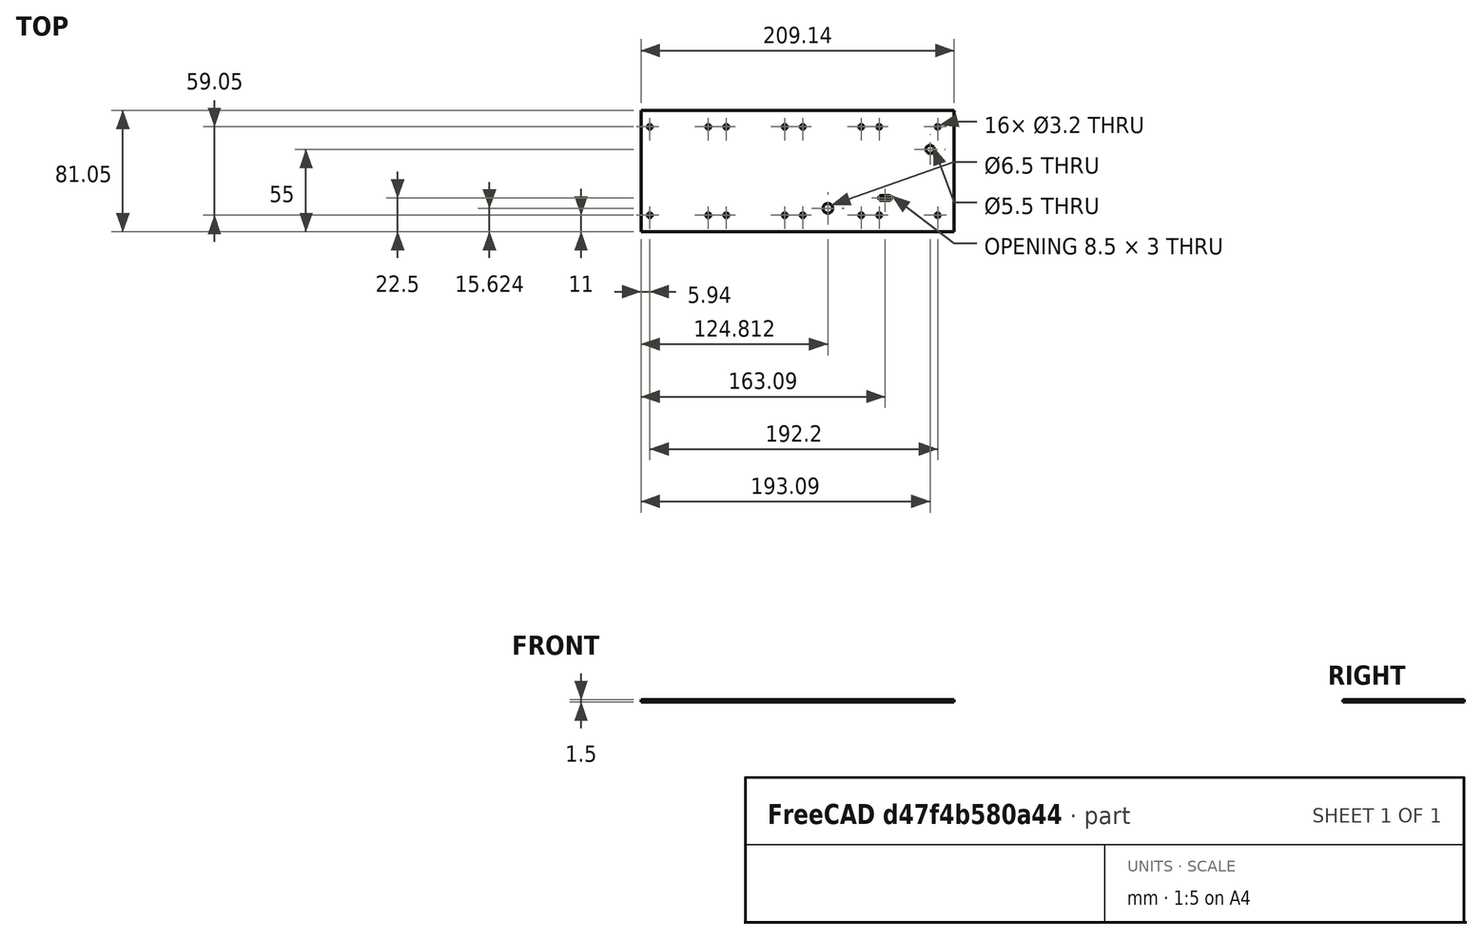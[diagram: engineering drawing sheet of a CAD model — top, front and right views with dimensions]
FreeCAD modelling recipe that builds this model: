
FCSTD DOCUMENT  (FreeCAD 0.21R33694 (Git))
Label: V1
License: All rights reserved
LicenseURL: https://en.wikipedia.org/wiki/All_rights_reserved
objects: Sketcher::SketchObject×1, App::VRMLObject×1, App::Part×1, PartDesign::Pad×1, PartDesign::Body×1
note: 4 computed .brp shape members not serialized (recipe doc carries the construction recipe); baked Part::Feature solids carry a one-line shape summary decoded from their .brp

FEATURE [Sketcher::SketchObject] Sketch
  FullyConstrained = false
  sketch-geometry (52):
    g0: LineSegment StartX=0 StartY=0 StartZ=0 EndX=209.14 EndY=0 EndZ=0
    g1: LineSegment StartX=209.14 StartY=0 StartZ=0 EndX=209.14 EndY=81.05 EndZ=0
    g2: LineSegment StartX=209.14 StartY=81.05 StartZ=0 EndX=0 EndY=81.05 EndZ=0
    g3: LineSegment StartX=0 StartY=81.05 StartZ=0 EndX=0 EndY=0 EndZ=0
    g4: Circle CenterX=5.94 CenterY=70.05 CenterZ=0 NormalX=0 NormalY=0 NormalZ=1 AngleXU=0 Radius=1.6
    g5: Circle CenterX=44.99 CenterY=70.05 CenterZ=0 NormalX=0 NormalY=0 NormalZ=1 AngleXU=0 Radius=1.6
    g6: Circle CenterX=56.99 CenterY=70.05 CenterZ=0 NormalX=0 NormalY=0 NormalZ=1 AngleXU=0 Radius=1.6
    g7: Circle CenterX=96.04 CenterY=70.05 CenterZ=0 NormalX=0 NormalY=0 NormalZ=1 AngleXU=0 Radius=1.6
    g8: Circle CenterX=108.04 CenterY=70.05 CenterZ=0 NormalX=0 NormalY=0 NormalZ=1 AngleXU=0 Radius=1.6
    g9: Circle CenterX=147.09 CenterY=70.05 CenterZ=0 NormalX=0 NormalY=0 NormalZ=1 AngleXU=0 Radius=1.6
    g10: Circle CenterX=159.09 CenterY=70.05 CenterZ=0 NormalX=0 NormalY=0 NormalZ=1 AngleXU=0 Radius=1.6
    g11: Circle CenterX=198.14 CenterY=70.05 CenterZ=0 NormalX=0 NormalY=0 NormalZ=1 AngleXU=0 Radius=1.6
    g12: LineSegment StartX=0 StartY=70.05 StartZ=0 EndX=209.14 EndY=70.05 EndZ=0
    g13: LineSegment StartX=0 StartY=11 StartZ=0 EndX=209.14 EndY=11 EndZ=0
    g14: LineSegment StartX=5.94 StartY=70.05 StartZ=0 EndX=5.94 EndY=11 EndZ=0
    g15: LineSegment StartX=44.99 StartY=70.05 StartZ=0 EndX=44.99 EndY=11 EndZ=0
    g16: LineSegment StartX=56.99 StartY=70.05 StartZ=0 EndX=56.99 EndY=11 EndZ=0
    g17: LineSegment StartX=96.04 StartY=70.05 StartZ=0 EndX=96.04 EndY=11 EndZ=0
    g18: LineSegment StartX=108.04 StartY=70.05 StartZ=0 EndX=108.04 EndY=11 EndZ=0
    g19: LineSegment StartX=147.09 StartY=70.05 StartZ=0 EndX=147.09 EndY=11 EndZ=0
    g20: LineSegment StartX=159.09 StartY=70.05 StartZ=0 EndX=159.09 EndY=11 EndZ=0
    g21: LineSegment StartX=198.14 StartY=70.05 StartZ=0 EndX=198.14 EndY=11 EndZ=0
    g22: Circle CenterX=198.14 CenterY=11 CenterZ=0 NormalX=0 NormalY=0 NormalZ=1 AngleXU=0 Radius=1.6
    g23: Circle CenterX=159.09 CenterY=11 CenterZ=0 NormalX=0 NormalY=0 NormalZ=1 AngleXU=0 Radius=1.6
    g24: Circle CenterX=147.09 CenterY=11 CenterZ=0 NormalX=0 NormalY=0 NormalZ=1 AngleXU=0 Radius=1.6
    g25: Circle CenterX=108.04 CenterY=11 CenterZ=0 NormalX=0 NormalY=0 NormalZ=1 AngleXU=0 Radius=1.6
    g26: Circle CenterX=96.04 CenterY=11 CenterZ=0 NormalX=0 NormalY=0 NormalZ=1 AngleXU=0 Radius=1.6
    g27: Circle CenterX=56.99 CenterY=11 CenterZ=0 NormalX=0 NormalY=0 NormalZ=1 AngleXU=0 Radius=1.6
    g28: Circle CenterX=44.99 CenterY=11 CenterZ=0 NormalX=0 NormalY=0 NormalZ=1 AngleXU=0 Radius=1.6
    g29: Circle CenterX=5.94 CenterY=11 CenterZ=0 NormalX=0 NormalY=0 NormalZ=1 AngleXU=0 Radius=1.6
    g30: LineSegment StartX=160.09 StartY=21 StartZ=0 EndX=166.09 EndY=21 EndZ=0
    g31: LineSegment StartX=160.09 StartY=24 StartZ=0 EndX=166.09 EndY=24 EndZ=0
    g32: LineSegment StartX=167.34 StartY=22.75 StartZ=0 EndX=167.34 EndY=22.25 EndZ=0
    g33: LineSegment StartX=158.84 StartY=22.75 StartZ=0 EndX=158.84 EndY=22.25 EndZ=0
    g34: LineSegment StartX=160.09 StartY=22.75 StartZ=0 EndX=166.09 EndY=22.75 EndZ=0
    g35: LineSegment StartX=166.09 StartY=22.75 StartZ=0 EndX=166.09 EndY=22.25 EndZ=0
    g36: LineSegment StartX=166.09 StartY=22.25 StartZ=0 EndX=160.09 EndY=22.25 EndZ=0
    g37: LineSegment StartX=160.09 StartY=22.25 StartZ=0 EndX=160.09 EndY=22.75 EndZ=0
    g38: ArcOfCircle CenterX=160.09 CenterY=22.75 CenterZ=0 NormalX=0 NormalY=0 NormalZ=1 AngleXU=0 Radius=1.25 StartAngle=1.5708 EndAngle=3.14159
    g39: ArcOfCircle CenterX=160.09 CenterY=22.25 CenterZ=0 NormalX=0 NormalY=0 NormalZ=1 AngleXU=0 Radius=1.25 StartAngle=3.14159 EndAngle=4.71239
    g40: ArcOfCircle CenterX=166.09 CenterY=22.75 CenterZ=0 NormalX=0 NormalY=0 NormalZ=1 AngleXU=0 Radius=1.25 StartAngle=-2.7e-15 EndAngle=1.5708
    g41: ArcOfCircle CenterX=166.09 CenterY=22.25 CenterZ=0 NormalX=0 NormalY=0 NormalZ=1 AngleXU=0 Radius=1.25 StartAngle=4.71239 EndAngle=6.28319
    g42: LineSegment StartX=160.09 StartY=22.75 StartZ=0 EndX=166.09 EndY=22.25 EndZ=0
    g43: GeomPoint X=163.09 Y=22.5 Z=0
    g44: LineSegment StartX=0 StartY=5 StartZ=0 EndX=204.14 EndY=5 EndZ=0
    g45: LineSegment StartX=204.14 StartY=5 StartZ=0 EndX=204.14 EndY=76.05 EndZ=0
    g46: LineSegment StartX=204.14 StartY=76.05 StartZ=0 EndX=0 EndY=76.05 EndZ=0
    g47: LineSegment StartX=50.99 StartY=76.05 StartZ=0 EndX=50.99 EndY=5 EndZ=0
    g48: LineSegment StartX=102.04 StartY=5 StartZ=0 EndX=102.04 EndY=76.05 EndZ=0
    g49: LineSegment StartX=153.09 StartY=76.05 StartZ=0 EndX=153.09 EndY=5 EndZ=0
    g50: Circle CenterX=193.09 CenterY=55 CenterZ=0 NormalX=0 NormalY=0 NormalZ=1 AngleXU=0 Radius=2.75
    g51: Circle CenterX=124.812 CenterY=15.6241 CenterZ=0 NormalX=0 NormalY=0 NormalZ=1 AngleXU=0 Radius=3.25
  constraints (141):
    c: Coincident(g0,g1)
    c: Coincident(g1,g2)
    c: Coincident(g2,g3)
    c: Coincident(g3,g0)
    c: Horizontal(g0)
    c: Horizontal(g2)
    c: Vertical(g1)
    c: Vertical(g3)
    c: Coincident(g0,g-1)
    c: Distance(g1) = 81.05
    c: Distance(g0) = 209.14
    c: PointOnObject(g12,g3)
    c: PointOnObject(g12,g1)
    c: Horizontal(g12)
    c: Distance(g1,g12) = 11
    c: PointOnObject(g4,g12)
    c: PointOnObject(g5,g12)
    c: PointOnObject(g6,g12)
    c: PointOnObject(g7,g12)
    c: PointOnObject(g8,g12)
    c: PointOnObject(g9,g12)
    c: PointOnObject(g10,g12)
    c: PointOnObject(g11,g12)
    c: Diameter(g11) = 3.2
    c: Equal(g11,g10)
    c: Equal(g10,g9)
    c: Equal(g9,g8)
    c: Equal(g8,g7)
    c: Equal(g7,g6)
    c: Equal(g6,g5)
    c: Equal(g5,g4)
    c: Distance(g4,g6) = 51.05
    c: Distance(g5,g7) = 51.05
    c: Distance(g4,g3) = 5.94
    c: Distance(g5,g6) = 12
    c: Distance(g7,g9) = 51.05
    c: Distance(g8,g10) = 51.05
    c: Distance(g8,g6) = 51.05
    c: Distance(g11,g9) = 51.05
    c: PointOnObject(g13,g3)
    c: PointOnObject(g13,g1)
    c: Horizontal(g13)
    c: Coincident(g14,g4)
    c: PointOnObject(g14,g13)
    c: Vertical(g14)
    c: Coincident(g15,g5)
    c: PointOnObject(g15,g13)
    c: Vertical(g15)
    c: Coincident(g16,g6)
    c: PointOnObject(g16,g13)
    c: Vertical(g16)
    c: Coincident(g17,g7)
    c: PointOnObject(g17,g13)
    c: Vertical(g17)
    c: Coincident(g18,g8)
    c: PointOnObject(g18,g13)
    c: Vertical(g18)
    c: Coincident(g19,g9)
    c: PointOnObject(g19,g13)
    c: Vertical(g19)
    c: Coincident(g20,g10)
    c: PointOnObject(g20,g13)
    c: Vertical(g20)
    c: Coincident(g21,g11)
    c: PointOnObject(g21,g13)
    c: Vertical(g21)
    c: Distance(g21,g0) = 11
    c: Coincident(g22,g21)
    c: Coincident(g23,g20)
    c: Coincident(g24,g19)
    c: Coincident(g25,g18)
    c: Coincident(g26,g17)
    c: Coincident(g27,g16)
    c: Coincident(g28,g15)
    c: Coincident(g29,g14)
    c: Equal(g11,g22)
    c: Equal(g22,g23)
    c: Equal(g23,g24)
    c: Equal(g24,g25)
    c: Equal(g25,g26)
    c: Equal(g26,g27)
    c: Equal(g27,g28)
    c: Equal(g28,g29)
    c: Horizontal(g30)
    c: Horizontal(g31)
    c: Vertical(g32)
    c: Vertical(g33)
    c: Coincident(g34,g35)
    c: Coincident(g35,g36)
    c: Coincident(g36,g37)
    c: Coincident(g37,g34)
    c: Horizontal(g34)
    c: Horizontal(g36)
    c: Vertical(g35)
    c: Vertical(g37)
    c: Coincident(g38,g34)
    c: Coincident(g39,g36)
    c: Coincident(g40,g34)
    c: Coincident(g41,g35)
    c: Coincident(g42,g38)
    c: Coincident(g42,g41)
    c: Symmetric(g38,g41,g43)
    c: PointOnObject(g44,g3)
    c: Horizontal(g44)
    c: Coincident(g45,g44)
    c: Vertical(g45)
    c: Coincident(g46,g45)
    c: PointOnObject(g46,g3)
    c: Horizontal(g46)
    c: Distance(g45) = 71.05
    c: PointOnObject(g47,g46)
    c: PointOnObject(g47,g44)
    c: Vertical(g47)
    c: PointOnObject(g48,g44)
    c: PointOnObject(g48,g46)
    c: Vertical(g48)
    c: PointOnObject(g49,g46)
    c: PointOnObject(g49,g44)
    c: Vertical(g49)
    c: Distance(g49,g45) = 51.05
    c: Distance(g49,g48) = 51.05
    c: Distance(g48,g47) = 51.05
    c: Distance(g47,g46) = 50.99
    c: Distance(g43,g44) = 17.5
    c: Distance(g44,g0) = 5
    c: Distance(g43,g49) = 10
    c: Tangent(g38,g33) = -1.5708
    c: Tangent(g38,g31) = 1.5708
    c: Tangent(g40,g31) = 1.5708
    c: Tangent(g40,g32) = 1.5708
    c: Tangent(g41,g32) = 1.5708
    c: Tangent(g41,g30) = -1.5708
    c: Tangent(g39,g30) = -1.5708
    c: Distance(g32,g33) = 8.5
    c: Coincident(g39,g33)
    c: Distance(g31,g30) = 3
    c: Distance(g32) = 0.5
    c: Distance(g50,g49) = 40
    c: Distance(g50,g44) = 50
    c: Diameter(g50) = 5.5
    c: Diameter(g51) = 6.5
FEATURE [App::VRMLObject] ControlBoard
FEATURE [App::Part] Part
  Group = -> [ControlBoard]
  Origin = -> Origin
  Placement = pos=(153.15,5,9.8) rot=(0,0,1;0rad)
FEATURE [PartDesign::Pad] Pad
  Direction = (0,0,1)
  Length = 1.5
  Length2 = 10
  Profile = -> Sketch
  ReferenceAxis = -> Sketch [N_Axis]
  Type = 0
FEATURE [PartDesign::Body] Body
  Group = -> [Sketch,Pad]
  Origin = -> Origin001
  Tip = -> Pad
